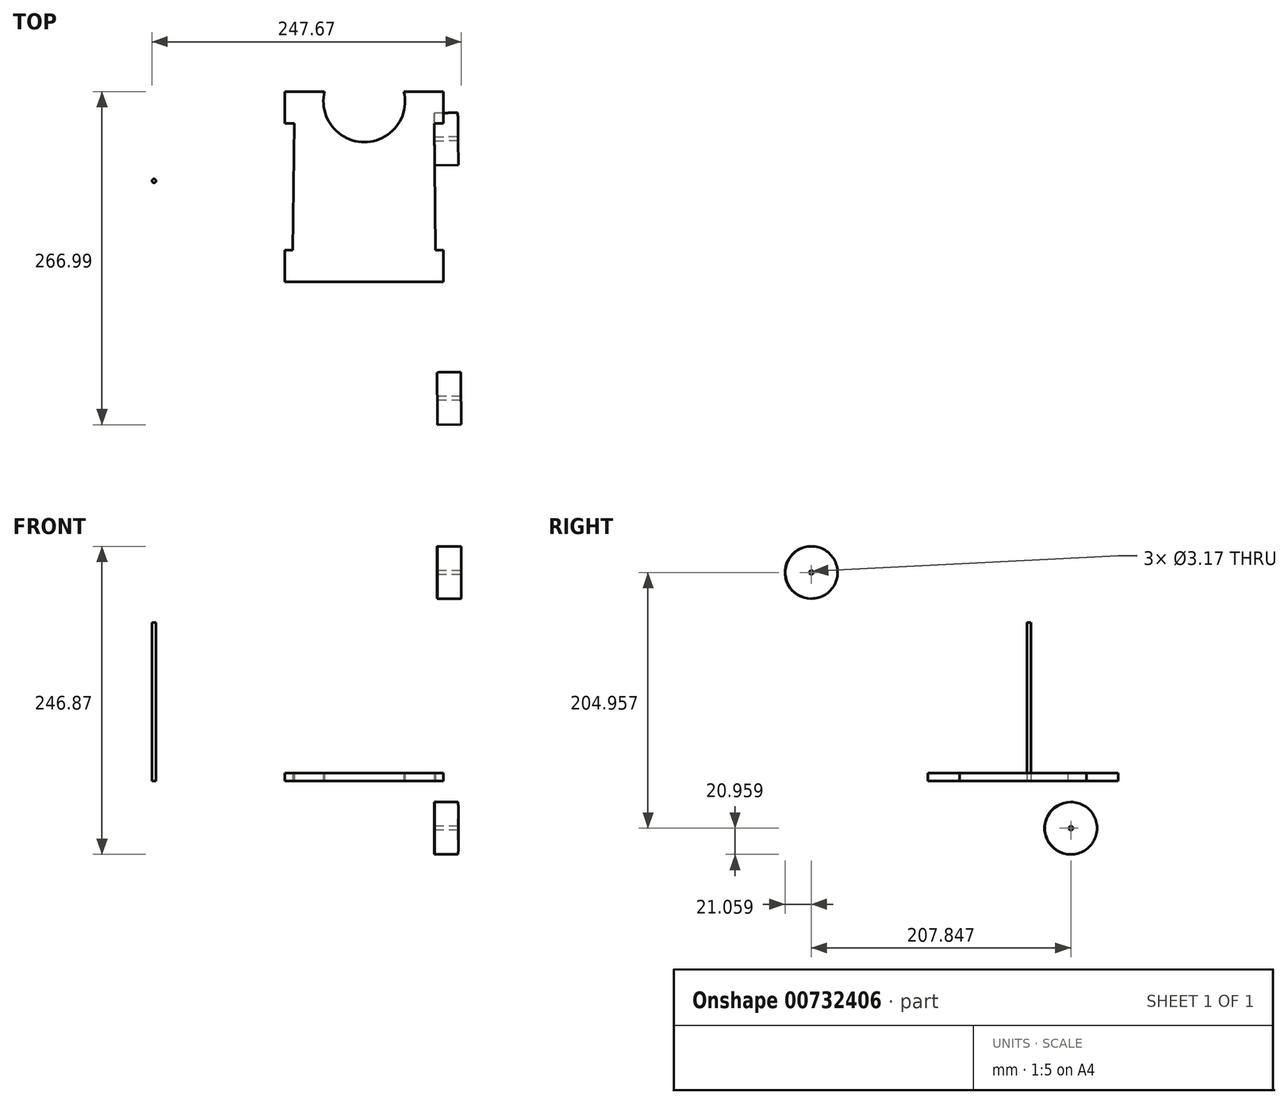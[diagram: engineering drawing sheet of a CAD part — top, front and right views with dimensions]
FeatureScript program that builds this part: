
annotation { "Feature Type Name" : "Feature", "Feature Type Description" : "" }
export const myFeature = defineFeature(function(context is Context, id is Id, definition is map)
    precondition{}
    {
        {
            var Q0;
            Q0=qCreatedBy(makeId("Top.planeOp"),FACE);
            var sketch = newSketch(context, id + "F0", { "sketchPlane" : qUnion([Q0])});
            skLineSegment(sketch, "E0.bottom", {"start": v(-54.27, 98.3) * mm, "end": v(72.73, 98.3) * mm});
            skLineSegment(sketch, "E0.top", {"start": v(-54.27, -54.1) * mm, "end": v(72.73, -54.1) * mm});
            skLineSegment(sketch, "E0.left", {"start": v(-54.27, 98.3) * mm, "end": v(-54.27, -54.1) * mm});
            skLineSegment(sketch, "E0.right", {"start": v(72.73, 98.3) * mm, "end": v(72.73, -54.1) * mm});
            skLineSegment(sketch, "E1", {"start": v(-46.79, 72.9) * mm, "end": v(-54.27, 72.9) * mm});
            skLineSegment(sketch, "E2", {"start": v(-54.27, 72.9) * mm, "end": v(-54.27, -28.7) * mm});
            skLineSegment(sketch, "E3", {"start": v(-54.27, -28.7) * mm, "end": v(-47.92, -28.7) * mm});
            skLineSegment(sketch, "E4", {"start": v(-47.92, -28.7) * mm, "end": v(-46.79, 72.9) * mm});
            skLineSegment(sketch, "E5", {"start": v(9.23, 98.3) * mm, "end": v(9.23, -54.1) * mm});
            skLineSegment(sketch, "E6.MirrorCS", {"start": v(65.25, 72.9) * mm, "end": v(72.73, 72.9) * mm});
            skLineSegment(sketch, "E7.MirrorCS", {"start": v(66.38, -28.7) * mm, "end": v(65.25, 72.9) * mm});
            skLineSegment(sketch, "E8.MirrorCS", {"start": v(72.73, -28.7) * mm, "end": v(66.38, -28.7) * mm});
            skLineSegment(sketch, "E9.MirrorCS", {"start": v(72.73, 72.9) * mm, "end": v(72.73, -28.7) * mm});
            skLineSegment(sketch, "E10.bottom", {"start": v(-40.93, 28.32) * mm, "end": v(-18.07, 28.32) * mm});
            skLineSegment(sketch, "E10.top", {"start": v(-40.93, -3.43) * mm, "end": v(-18.07, -3.43) * mm});
            skLineSegment(sketch, "E10.left", {"start": v(-40.93, 28.32) * mm, "end": v(-40.93, -3.43) * mm});
            skLineSegment(sketch, "E10.right", {"start": v(-18.07, 28.32) * mm, "end": v(-18.07, -3.43) * mm});
            skLineSegment(sketch, "E11.MirrorCS", {"start": v(59.4, 28.32) * mm, "end": v(36.54, 28.32) * mm});
            skLineSegment(sketch, "E12.MirrorCS", {"start": v(36.54, 28.32) * mm, "end": v(36.54, -3.43) * mm});
            skLineSegment(sketch, "E13.MirrorCS", {"start": v(59.4, -3.43) * mm, "end": v(36.54, -3.43) * mm});
            skLineSegment(sketch, "E14.MirrorCS", {"start": v(59.4, 28.32) * mm, "end": v(59.4, -3.43) * mm});
            skLineSegment(sketch, "E15.bottom", {"start": v(-14.9, -16.13) * mm, "end": v(33.36, -16.13) * mm});
            skLineSegment(sketch, "E15.top", {"start": v(-14.9, -41.53) * mm, "end": v(33.36, -41.53) * mm});
            skLineSegment(sketch, "E15.left", {"start": v(-14.9, -16.13) * mm, "end": v(-14.9, -41.53) * mm});
            skLineSegment(sketch, "E15.right", {"start": v(33.36, -16.13) * mm, "end": v(33.36, -41.53) * mm});
            skLineSegment(sketch, "E16.bottom", {"start": v(-14.9, -9.78) * mm, "end": v(33.36, -9.78) * mm});
            skLineSegment(sketch, "E16.top", {"start": v(-14.9, 66.42) * mm, "end": v(33.36, 66.42) * mm});
            skLineSegment(sketch, "E16.left", {"start": v(-14.9, -9.78) * mm, "end": v(-14.9, 66.42) * mm});
            skLineSegment(sketch, "E16.right", {"start": v(33.36, -9.78) * mm, "end": v(33.36, 66.42) * mm});
            skArc(sketch, "E17", {"start": v(-22.52, 98.3) * mm, "mid": v(9.23, 57.8) * mm, "end": v(40.98, 98.3) * mm});
            skSolve(sketch);
        }
        {
            var Q0;
            {var subQ12=sQuery(id+"F0.wireOp",EDGE,"E6.MirrorCS");Q0=makeQuery(id+"F0.imprint","IMPRINT",FACE,{"disambiguationData":[TD([[makeQuery(id+"F0.imprint","IMPRINT",EDGE,{"derivedFrom":subQ12}),1.0]])]});}
            var Q1;
            {var subQ12=sQuery(id+"F0.wireOp",EDGE,"E1");Q1=makeQuery(id+"F0.imprint","IMPRINT",FACE,{"disambiguationData":[TD([[makeQuery(id+"F0.imprint","IMPRINT",EDGE,{"derivedFrom":subQ12}),-1.0]])]});}
            var Q2;
            {var subQ5=sQuery(id+"F0.wireOp",EDGE,"E15.left");Q2=makeQuery(id+"F0.imprint","IMPRINT",FACE,{"disambiguationData":[TD([[makeQuery(id+"F0.imprint","IMPRINT",EDGE,{"derivedFrom":subQ5}),1.0]])]});}
            var Q3;
            {var subQ5=sQuery(id+"F0.wireOp",EDGE,"E15.right");Q3=makeQuery(id+"F0.imprint","IMPRINT",FACE,{"disambiguationData":[TD([[makeQuery(id+"F0.imprint","IMPRINT",EDGE,{"derivedFrom":subQ5}),-1.0]])]});}
            var Q4;
            {var subQ5=sQuery(id+"F0.wireOp",EDGE,"E16.right");Q4=makeQuery(id+"F0.imprint","IMPRINT",FACE,{"disambiguationData":[TD([[makeQuery(id+"F0.imprint","IMPRINT",EDGE,{"derivedFrom":subQ5}),1.0]])]});}
            var Q5;
            {var subQ5=sQuery(id+"F0.wireOp",EDGE,"E16.left");Q5=makeQuery(id+"F0.imprint","IMPRINT",FACE,{"disambiguationData":[TD([[makeQuery(id+"F0.imprint","IMPRINT",EDGE,{"derivedFrom":subQ5}),-1.0]])]});}
            var Q6;
            Q6=makeQuery(id+"F0.imprint","IMPRINT",FACE,{"disambiguationData":[TD([[makeQuery(id+"F0.imprint","IMPRINT",EDGE,{"derivedFrom":sQuery(id+"F0.wireOp",EDGE,"E10.bottom")}),-1.0]])]});
            var Q7;
            Q7=makeQuery(id+"F0.imprint","IMPRINT",FACE,{"disambiguationData":[TD([[makeQuery(id+"F0.imprint","IMPRINT",EDGE,{"derivedFrom":sQuery(id+"F0.wireOp",EDGE,"E11.MirrorCS")}),1.0]])]});
            extrude(context, id + "F1", {"entities" : qUnion([Q0, Q1, Q2, Q3, Q4, Q5, Q6, Q7]), "depth" : 6.35 * mm, "offsetDistance" : 25.4 * mm});
        }
        {
            var Q0;
            Q0=makeQuery(id+"F1.opExtrude","SWEPT_FACE",FACE,{"disambiguationData":[OSD([sQuery(id+"F0.wireOp",EDGE,"E7.MirrorCS")])]});
            var sketch = newSketch(context, id + "F2", { "sketchPlane" : qUnion([Q0])});
            skCircle(sketch, "E18", {"center": v(59.37, -37.74) * mm, "radius": 20.96 * mm});
            skCircle(sketch, "E19", {"center": v(-148.5, 167.22) * mm, "radius": 20.96 * mm});
            skCircle(sketch, "E20", {"center": v(-148.5, 167.22) * mm, "radius": 1.59 * mm});
            skCircle(sketch, "E21", {"center": v(59.37, -37.74) * mm, "radius": 1.59 * mm});
            skSolve(sketch);
        }
        {
            var Q0;
            {var subQ0=sQuery(id+"F2.wireOp",EDGE,"E18");var subQ1=makeQuery(id+"F1.opExtrude","CAP_EDGE",EDGE,{"disambiguationData":[OSD([sQuery(id+"F0.wireOp",EDGE,"E7.MirrorCS")])],"isStart":false});var subQ2=makeQuery(id+"F2.imprint","INTERSECT",VERTEX,{"disambiguationData":[OD(0.0)],"derivedFrom":[subQ1,subQ0]});Q0=makeQuery(id+"F2.imprint","IMPRINT",FACE,{"disambiguationData":[TD([[makeQuery(id+"F2.imprint","IMPRINT",EDGE,{"disambiguationData":[TD([[subQ2,1.0]])],"derivedFrom":subQ0}),1.0]])]});}
            var Q1;
            {var subQ0=sQuery(id+"F2.wireOp",EDGE,"E18");var subQ1=makeQuery(id+"F1.opExtrude","CAP_EDGE",EDGE,{"disambiguationData":[OSD([sQuery(id+"F0.wireOp",EDGE,"E7.MirrorCS")])],"isStart":true});var subQ2=makeQuery(id+"F2.imprint","INTERSECT",VERTEX,{"disambiguationData":[OD(0.0)],"derivedFrom":[subQ1,subQ0]});Q1=makeQuery(id+"F2.imprint","IMPRINT",FACE,{"disambiguationData":[TD([[makeQuery(id+"F2.imprint","IMPRINT",EDGE,{"disambiguationData":[TD([[subQ2,-1.0]])],"derivedFrom":subQ0}),1.0]])]});}
            var Q2;
            {var subQ0=sQuery(id+"F2.wireOp",EDGE,"E18");var subQ1=sQuery(id+"F0.wireOp",EDGE,"E7.MirrorCS");var subQ2=makeQuery(id+"F1.opExtrude","CAP_EDGE",EDGE,{"disambiguationData":[OSD([subQ1])],"isStart":false});var subQ3=makeQuery(id+"F2.imprint","INTERSECT",VERTEX,{"disambiguationData":[OD(0.0)],"derivedFrom":[subQ2,subQ0]});Q2=makeQuery(id+"F2.imprint","IMPRINT",FACE,{"disambiguationData":[TD([[makeQuery(id+"F2.imprint","IMPRINT",EDGE,{"disambiguationData":[TD([[subQ3,-1.0]])],"derivedFrom":subQ0}),1.0]])]});}
            extrude(context, id + "F3", {"entities" : qUnion([Q0, Q1, Q2]), "operationType" : NewBodyOperationType.ADD, "depth" : 19 * mm, "offsetDistance" : 25.4 * mm});
        }
        {
            var Q0;
            Q0 = qSketchRegion(id + "F2", true);
            extrude(context, id + "F4", {"entities" : qUnion([Q0]), "depth" : 19 * mm, "offsetDistance" : 25.4 * mm});
        }
        {
            var Q0;
            Q0=qCreatedBy(makeId("Top.planeOp"),FACE);
            var sketch = newSketch(context, id + "F5", { "sketchPlane" : qUnion([Q0])});
            skCircle(sketch, "E22", {"center": v(-159.15, 26.7) * mm, "radius": 1.59 * mm});
            skSolve(sketch);
        }
        {
            var Q0;
            Q0=makeQuery(id+"F5.imprint","IMPRINT",FACE,{"disambiguationData":[TD([[makeQuery(id+"F5.imprint","IMPRINT",EDGE,{"derivedFrom":sQuery(id+"F5.wireOp",EDGE,"E22")}),1.0]])]});
            extrude(context, id + "F6", {"entities" : qUnion([Q0]), "depth" : 127 * mm, "offsetDistance" : 25.4 * mm});
        }
    });
